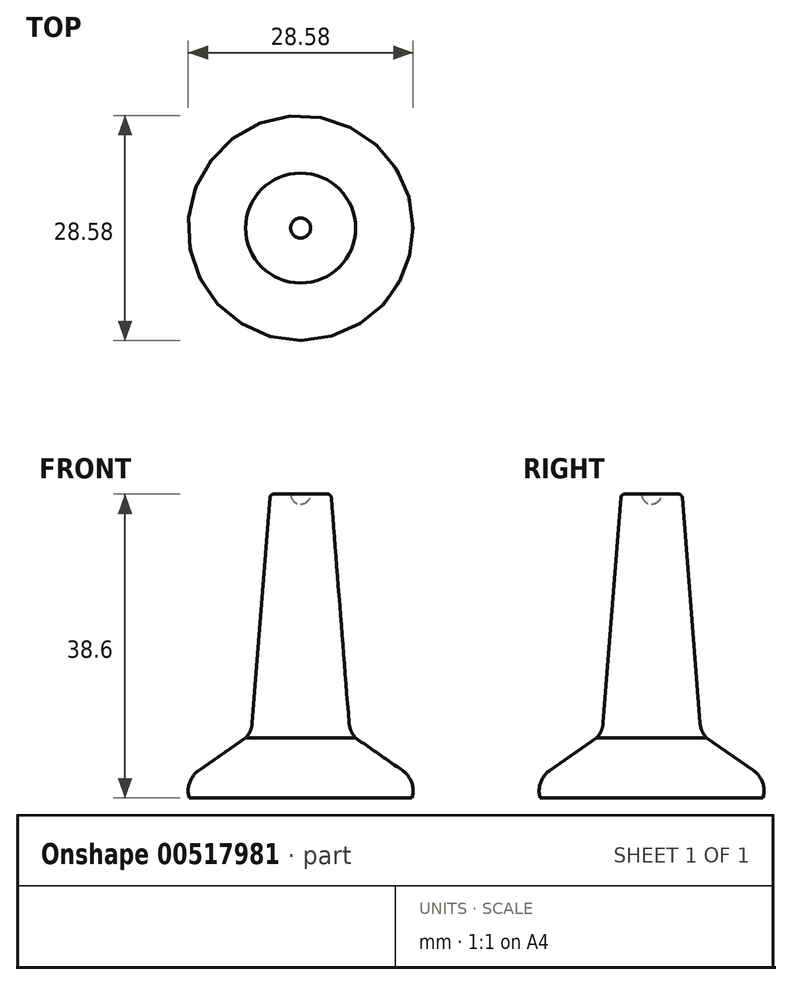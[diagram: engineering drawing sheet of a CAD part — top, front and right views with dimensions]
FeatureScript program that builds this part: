
annotation { "Feature Type Name" : "Feature", "Feature Type Description" : "" }
export const myFeature = defineFeature(function(context is Context, id is Id, definition is map)
    precondition{}
    {
        {
            var Q0;
            Q0=qCreatedBy(makeId("Right.planeOp"),FACE);
            var sketch = newSketch(context, id + "F0", { "sketchPlane" : qUnion([Q0])});
            skLineSegment(sketch, "E0", {"start": v(1.27, 39.5) * mm, "end": v(3.4, 39.5) * mm});
            skLineSegment(sketch, "E1", {"start": v(3.9, 39.03) * mm, "end": v(6.15, 10.42) * mm});
            skArc(sketch, "E2.filletArc", {"start": v(6.15, 10.42) * mm, "mid": v(6.4, 9.4) * mm, "end": v(6.99, 8.5) * mm});
            skLineSegment(sketch, "E3", {"start": v(12.93, 4.38) * mm, "end": v(6.99, 8.5) * mm});
            skArc(sketch, "E4.filletArc", {"start": v(14.16, 0.89) * mm, "mid": v(14.1, 2.83) * mm, "end": v(12.93, 4.38) * mm});
            skLineSegment(sketch, "E5", {"start": v(14.16, 0.89) * mm, "end": v(0, 0.89) * mm});
            skPoint(sketch, "E6.visualSharp", {"position": v(3.86, 39.5) * mm});
            skArc(sketch, "E6.filletArc", {"start": v(3.9, 39.03) * mm, "mid": v(3.74, 39.36) * mm, "end": v(3.4, 39.5) * mm});
            skArc(sketch, "E7", {"start": v(0, 38.22) * mm, "mid": v(0.9, 38.6) * mm, "end": v(1.27, 39.5) * mm});
            skLineSegment(sketch, "E8", {"start": v(0, 38.22) * mm, "end": v(0, 0.89) * mm});
            skSolve(sketch);
        }
        {
            var Q0;
            Q0 = qSketchRegion(id + "F0", true);
            var Q1;
            Q1=sQuery(id+"F0.wireOp",EDGE,"E8");
            revolve(context, id + "F1", {"entities" : qUnion([Q0]), "axis" : qUnion([Q1]), "revolveType" : RevolveType.FULL});
        }
    });
